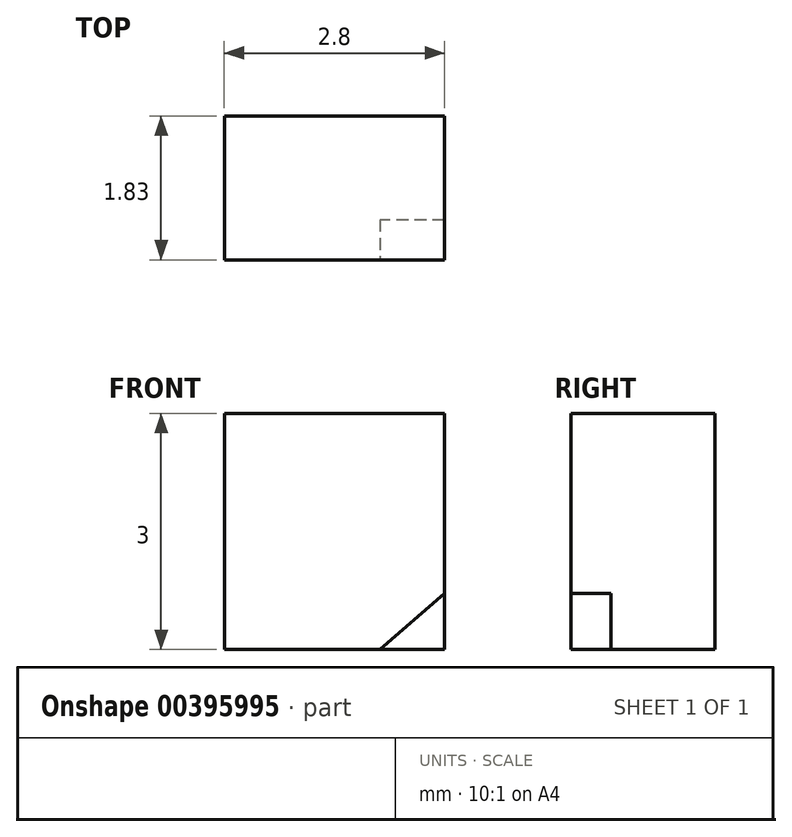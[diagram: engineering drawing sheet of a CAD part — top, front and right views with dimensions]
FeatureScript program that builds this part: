
annotation { "Feature Type Name" : "Feature", "Feature Type Description" : "" }
export const myFeature = defineFeature(function(context is Context, id is Id, definition is map)
    precondition{}
    {
        {
            var Q0;
            Q0=qCreatedBy(makeId("Front.planeOp"),FACE);
            var sketch = newSketch(context, id + "F0", { "sketchPlane" : qUnion([Q0])});
            skLineSegment(sketch, "E0.bottom", {"start": v(1.4, -1.5) * mm, "end": v(-1.4, -1.5) * mm});
            skLineSegment(sketch, "E0.top", {"start": v(1.4, 1.5) * mm, "end": v(-1.4, 1.5) * mm});
            skLineSegment(sketch, "E0.left", {"start": v(1.4, -1.5) * mm, "end": v(1.4, 1.5) * mm});
            skLineSegment(sketch, "E0.right", {"start": v(-1.4, -1.5) * mm, "end": v(-1.4, 1.5) * mm});
            skPoint(sketch, "E0.middle", {"position": v(0, 0) * mm});
            skSolve(sketch);
        }
        {
            var Q0;
            Q0=makeQuery(id+"F0.imprint","IMPRINT",FACE,{"disambiguationData":[TD([[makeQuery(id+"F0.imprint","IMPRINT",EDGE,{"derivedFrom":sQuery(id+"F0.wireOp",EDGE,"E0.bottom")}),-1.0]])]});
            extrude(context, id + "F1", {"entities" : qUnion([Q0]), "depth" : 1.83 * mm});
        }
        {
            var Q0;
            Q0=makeQuery(id+"F1.opExtrude","CAP_FACE",FACE,{"disambiguationData":[OSD([sQuery(id+"F0.wireOp",EDGE,"E0.bottom"),sQuery(id+"F0.wireOp",EDGE,"E0.top"),sQuery(id+"F0.wireOp",EDGE,"E0.left"),sQuery(id+"F0.wireOp",EDGE,"E0.right")])],"isStart":false});
            var sketch = newSketch(context, id + "F2", { "sketchPlane" : qUnion([Q0])});
            skLineSegment(sketch, "E1", {"start": v(0.49, -1.58) * mm, "end": v(1.5, -0.7) * mm});
            skLineSegment(sketch, "E2", {"start": v(1.5, -0.7) * mm, "end": v(1.5, -1.59) * mm});
            skLineSegment(sketch, "E3", {"start": v(1.5, -1.59) * mm, "end": v(0.49, -1.58) * mm});
            skSolve(sketch);
        }
        {
            var Q0;
            Q0 = qSketchRegion(id + "F2", true);
            extrude(context, id + "F3", {"entities" : qUnion([Q0]), "operationType" : NewBodyOperationType.REMOVE, "oppositeDirection" : true, "depth" : 0.5 * mm});
        }
    });
